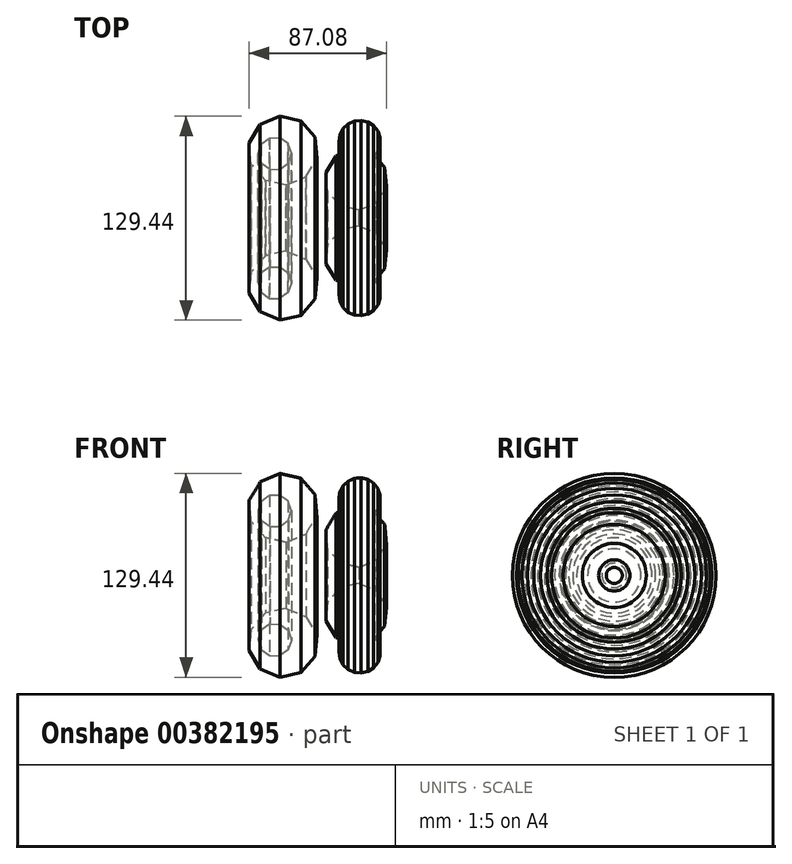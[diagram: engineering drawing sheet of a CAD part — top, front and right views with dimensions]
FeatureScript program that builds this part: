
annotation { "Feature Type Name" : "Feature", "Feature Type Description" : "" }
export const myFeature = defineFeature(function(context is Context, id is Id, definition is map)
    precondition{}
    {
        {
            var Q0;
            Q0=qCreatedBy(makeId("Front.planeOp"),FACE);
            var sketch = newSketch(context, id + "F0", { "sketchPlane" : qUnion([Q0])});
            skLineSegment(sketch, "E0", {"start": v(-55.89, 0) * mm, "end": v(60.06, 0) * mm, "construction": true});
            skCircle(sketch, "E1.cCircle", {"center": v(-64.78, 41) * mm, "radius": 9.98 * mm, "construction": true});
            skLineSegment(sketch, "E1.0", {"start": v(-56.4, 47.34) * mm, "end": v(-54.28, 41.2) * mm});
            skLineSegment(sketch, "E1.1", {"start": v(-54.28, 41.2) * mm, "end": v(-56.17, 35) * mm});
            skLineSegment(sketch, "E1.2", {"start": v(-56.17, 35) * mm, "end": v(-61.34, 31.09) * mm});
            skLineSegment(sketch, "E1.3", {"start": v(-61.34, 31.09) * mm, "end": v(-67.83, 30.96) * mm});
            skLineSegment(sketch, "E1.4", {"start": v(-67.83, 30.96) * mm, "end": v(-73.15, 34.68) * mm});
            skLineSegment(sketch, "E1.5", {"start": v(-73.15, 34.68) * mm, "end": v(-75.27, 40.8) * mm});
            skLineSegment(sketch, "E1.6", {"start": v(-75.27, 40.8) * mm, "end": v(-73.39, 47.02) * mm});
            skLineSegment(sketch, "E1.7", {"start": v(-73.39, 47.02) * mm, "end": v(-68.21, 50.93) * mm});
            skLineSegment(sketch, "E1.8", {"start": v(-68.21, 50.93) * mm, "end": v(-61.73, 51.05) * mm});
            skLineSegment(sketch, "E1.9", {"start": v(-61.73, 51.05) * mm, "end": v(-56.4, 47.34) * mm});
            skPoint(sketch, "E1.0.midPoint", {"position": v(-55.34, 44.27) * mm});
            skCircle(sketch, "E2.cCircle", {"center": v(-59.52, 42.82) * mm, "radius": 20.91 * mm, "construction": true});
            skLineSegment(sketch, "E2.0", {"start": v(-38.07, 37.95) * mm, "end": v(-45.03, 26.28) * mm});
            skLineSegment(sketch, "E2.1", {"start": v(-45.03, 26.28) * mm, "end": v(-57.52, 20.93) * mm});
            skLineSegment(sketch, "E2.2", {"start": v(-57.52, 20.93) * mm, "end": v(-70.77, 23.93) * mm});
            skLineSegment(sketch, "E2.3", {"start": v(-70.77, 23.93) * mm, "end": v(-79.73, 34.16) * mm});
            skLineSegment(sketch, "E2.4", {"start": v(-79.73, 34.16) * mm, "end": v(-80.96, 47.7) * mm});
            skLineSegment(sketch, "E2.5", {"start": v(-80.96, 47.7) * mm, "end": v(-74, 59.36) * mm});
            skLineSegment(sketch, "E2.6", {"start": v(-74, 59.36) * mm, "end": v(-61.51, 64.72) * mm});
            skLineSegment(sketch, "E2.7", {"start": v(-61.51, 64.72) * mm, "end": v(-48.26, 61.71) * mm});
            skLineSegment(sketch, "E2.8", {"start": v(-48.26, 61.71) * mm, "end": v(-39.3, 51.49) * mm});
            skLineSegment(sketch, "E2.9", {"start": v(-39.3, 51.49) * mm, "end": v(-38.07, 37.95) * mm});
            skPoint(sketch, "E2.0.midPoint", {"position": v(-41.55, 32.12) * mm});
            skCircle(sketch, "E3.cCircle", {"center": v(-13.06, 24.68) * mm, "radius": 18.7 * mm, "construction": true});
            skLineSegment(sketch, "E3.0", {"start": v(-32.24, 29.03) * mm, "end": v(-26.02, 39.47) * mm});
            skLineSegment(sketch, "E3.1", {"start": v(-26.02, 39.47) * mm, "end": v(-14.85, 44.26) * mm});
            skLineSegment(sketch, "E3.2", {"start": v(-14.85, 44.26) * mm, "end": v(-3, 41.57) * mm});
            skLineSegment(sketch, "E3.3", {"start": v(-3, 41.57) * mm, "end": v(5.01, 32.43) * mm});
            skLineSegment(sketch, "E3.4", {"start": v(5.01, 32.43) * mm, "end": v(6.12, 20.32) * mm});
            skLineSegment(sketch, "E3.5", {"start": v(6.12, 20.32) * mm, "end": v(-0.1, 9.88) * mm});
            skLineSegment(sketch, "E3.6", {"start": v(-0.1, 9.88) * mm, "end": v(-11.28, 5.09) * mm});
            skLineSegment(sketch, "E3.7", {"start": v(-11.28, 5.09) * mm, "end": v(-23.13, 7.78) * mm});
            skLineSegment(sketch, "E3.8", {"start": v(-23.13, 7.78) * mm, "end": v(-31.14, 16.93) * mm});
            skLineSegment(sketch, "E3.9", {"start": v(-31.14, 16.93) * mm, "end": v(-32.24, 29.03) * mm});
            skPoint(sketch, "E3.0.midPoint", {"position": v(-29.13, 34.25) * mm});
            skCircle(sketch, "E4.cCircle", {"center": v(-10.89, 48.81) * mm, "radius": 13.06 * mm, "construction": true});
            skLineSegment(sketch, "E4.0", {"start": v(-1.82, 39.16) * mm, "end": v(-5.44, 36.74) * mm});
            skLineSegment(sketch, "E4.1", {"start": v(-5.44, 36.74) * mm, "end": v(-9.65, 35.63) * mm});
            skLineSegment(sketch, "E4.2", {"start": v(-9.65, 35.63) * mm, "end": v(-14, 35.94) * mm});
            skLineSegment(sketch, "E4.3", {"start": v(-14, 35.94) * mm, "end": v(-18.01, 37.65) * mm});
            skLineSegment(sketch, "E4.4", {"start": v(-18.01, 37.65) * mm, "end": v(-21.25, 40.57) * mm});
            skLineSegment(sketch, "E4.5", {"start": v(-21.25, 40.57) * mm, "end": v(-23.36, 44.38) * mm});
            skLineSegment(sketch, "E4.6", {"start": v(-23.36, 44.38) * mm, "end": v(-24.13, 48.67) * mm});
            skLineSegment(sketch, "E4.7", {"start": v(-24.13, 48.67) * mm, "end": v(-23.45, 52.98) * mm});
            skLineSegment(sketch, "E4.8", {"start": v(-23.45, 52.98) * mm, "end": v(-21.42, 56.83) * mm});
            skLineSegment(sketch, "E4.9", {"start": v(-21.42, 56.83) * mm, "end": v(-18.25, 59.82) * mm});
            skLineSegment(sketch, "E4.10", {"start": v(-18.25, 59.82) * mm, "end": v(-14.27, 61.61) * mm});
            skLineSegment(sketch, "E4.11", {"start": v(-14.27, 61.61) * mm, "end": v(-9.93, 62.02) * mm});
            skLineSegment(sketch, "E4.12", {"start": v(-9.93, 62.02) * mm, "end": v(-5.7, 61) * mm});
            skLineSegment(sketch, "E4.13", {"start": v(-5.7, 61) * mm, "end": v(-2.02, 58.65) * mm});
            skLineSegment(sketch, "E4.14", {"start": v(-2.02, 58.65) * mm, "end": v(0.69, 55.23) * mm});
            skLineSegment(sketch, "E4.15", {"start": v(0.69, 55.23) * mm, "end": v(2.15, 51.13) * mm});
            skLineSegment(sketch, "E4.16", {"start": v(2.15, 51.13) * mm, "end": v(2.2, 46.77) * mm});
            skLineSegment(sketch, "E4.17", {"start": v(2.2, 46.77) * mm, "end": v(0.82, 42.63) * mm});
            skLineSegment(sketch, "E4.18", {"start": v(0.82, 42.63) * mm, "end": v(-1.82, 39.16) * mm});
            skPoint(sketch, "E4.0.midPoint", {"position": v(-3.63, 37.95) * mm});
            skSolve(sketch);
        }
        {
            var Q0;
            Q0 = qSketchRegion(id + "F0", true);
            var Q1;
            Q1=sQuery(id+"F0.wireOp",EDGE,"E0");
            revolve(context, id + "F1", {"entities" : qUnion([Q0]), "axis" : qUnion([Q1]), "revolveType" : RevolveType.FULL});
        }
    });
